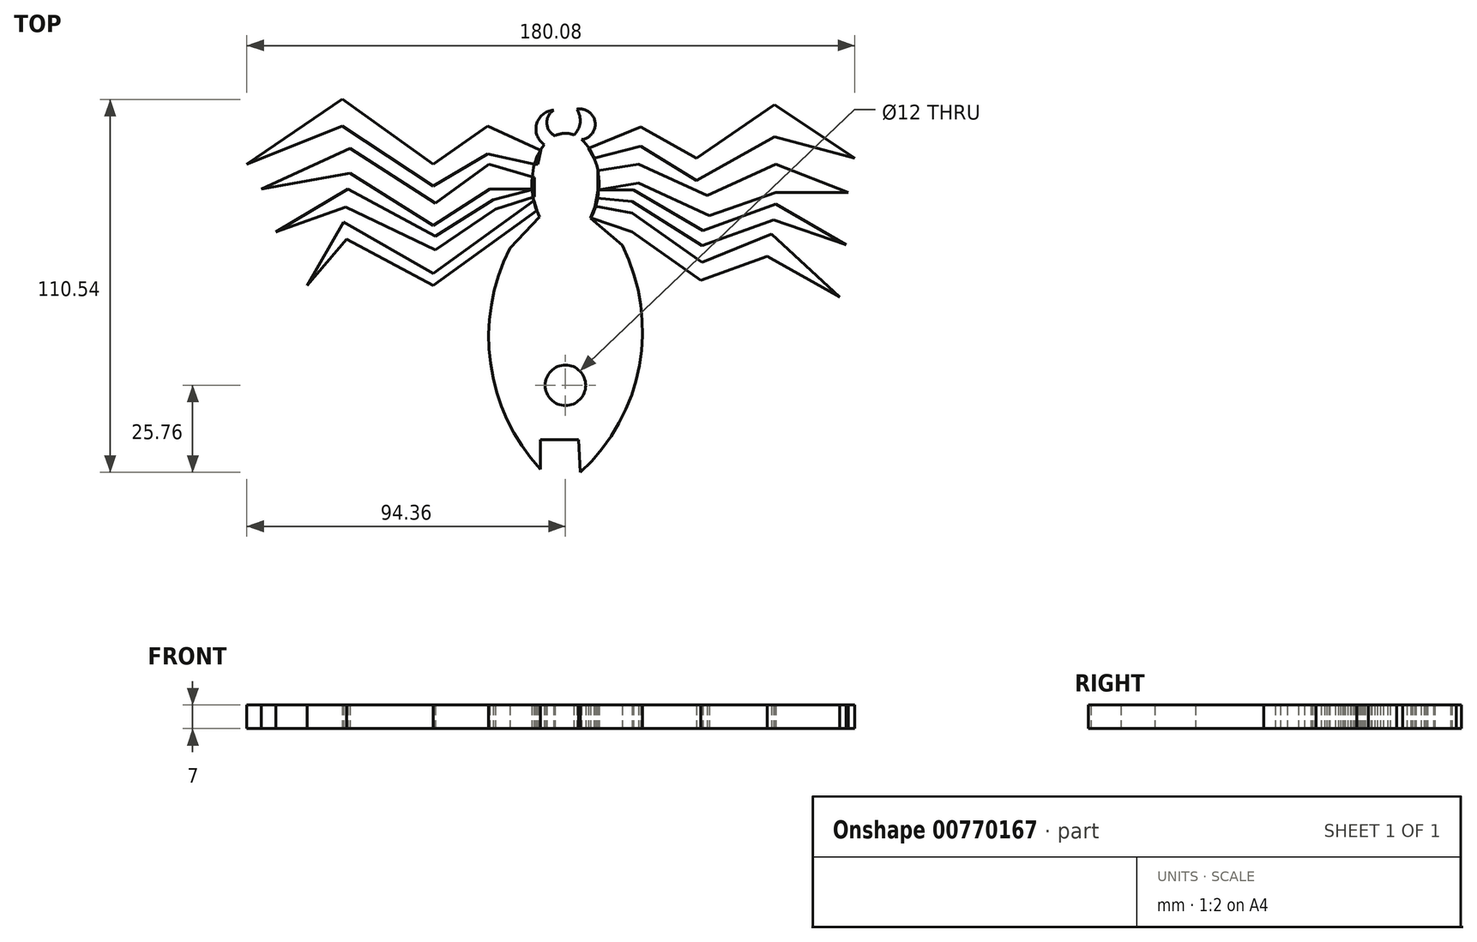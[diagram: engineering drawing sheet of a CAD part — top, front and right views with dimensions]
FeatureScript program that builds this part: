
annotation { "Feature Type Name" : "Feature", "Feature Type Description" : "" }
export const myFeature = defineFeature(function(context is Context, id is Id, definition is map)
    precondition{}
    {
        {
            var Q0;
            Q0=qCreatedBy(makeId("Top.planeOp"),FACE);
            var sketch = newSketch(context, id + "F0", { "sketchPlane" : qUnion([Q0])});
            skEllipse(sketch, "E0", {"center": v(0, 59.61) * mm, "majorRadius": 15.1 * mm, "minorRadius": 9.95 * mm, "majorAxis": v(0, 1)});
            skLineSegment(sketch, "E1", {"start": v(-7.66, 49.96) * mm, "end": v(-16.4, 40.68) * mm});
            skLineSegment(sketch, "E2", {"start": v(7.4, 49.5) * mm, "end": v(16.79, 41.5) * mm});
            skArc(sketch, "E3", {"start": v(-16.4, 40.68) * mm, "mid": v(-22.18, 6.45) * mm, "end": v(-7.36, -24.94) * mm});
            skArc(sketch, "E4", {"start": v(4.44, -25.76) * mm, "mid": v(21.9, 5.8) * mm, "end": v(16.79, 41.5) * mm});
            skLineSegment(sketch, "E5", {"start": v(-7.36, -24.94) * mm, "end": v(-7.36, -16.15) * mm});
            skLineSegment(sketch, "E6", {"start": v(-7.36, -16.15) * mm, "end": v(3.9, -16.15) * mm});
            skLineSegment(sketch, "E7", {"start": v(3.9, -16.15) * mm, "end": v(4.44, -25.76) * mm});
            skArc(sketch, "E8", {"start": v(-3.53, 81.58) * mm, "mid": v(-8.55, 77.44) * mm, "end": v(-6.26, 71.35) * mm});
            skArc(sketch, "E9", {"start": v(4.8, 72.85) * mm, "mid": v(8.77, 78.1) * mm, "end": v(3.34, 81.85) * mm});
            skArc(sketch, "E10", {"start": v(-3.53, 81.58) * mm, "mid": v(-5.49, 77.65) * mm, "end": v(-3.15, 73.93) * mm});
            skArc(sketch, "E11", {"start": v(0, 72.85) * mm, "mid": v(4.01, 76.48) * mm, "end": v(3.34, 81.85) * mm});
            skCircle(sketch, "E12", {"center": v(0, 0) * mm, "radius": 6 * mm});
            skSolve(sketch);
        }
        {
            var Q0;
            Q0=qCreatedBy(makeId("Top.planeOp"),FACE);
            var sketch = newSketch(context, id + "F1", { "sketchPlane" : qUnion([Q0])});
            skLineSegment(sketch, "E13", {"start": v(-7.74, 69.88) * mm, "end": v(-22.97, 76.86) * mm});
            skLineSegment(sketch, "E14", {"start": v(-22.97, 76.86) * mm, "end": v(-39.13, 65.6) * mm});
            skLineSegment(sketch, "E15", {"start": v(-39.13, 65.6) * mm, "end": v(-66.07, 84.78) * mm});
            skLineSegment(sketch, "E16", {"start": v(-66.07, 84.78) * mm, "end": v(-94.36, 65.6) * mm});
            skLineSegment(sketch, "E17", {"start": v(-94.36, 65.6) * mm, "end": v(-66.07, 76.86) * mm});
            skLineSegment(sketch, "E18", {"start": v(-66.07, 76.86) * mm, "end": v(-39.13, 59.12) * mm});
            skLineSegment(sketch, "E19", {"start": v(-39.13, 59.12) * mm, "end": v(-22.97, 68.62) * mm});
            skLineSegment(sketch, "E20", {"start": v(-22.97, 68.62) * mm, "end": v(-9.2, 65.6) * mm});
            skLineSegment(sketch, "E21", {"start": v(6.81, 70.2) * mm, "end": v(22.34, 76.54) * mm});
            skLineSegment(sketch, "E22", {"start": v(22.34, 76.54) * mm, "end": v(38.82, 67.35) * mm});
            skLineSegment(sketch, "E23", {"start": v(38.82, 67.35) * mm, "end": v(61.95, 83.2) * mm});
            skLineSegment(sketch, "E24", {"start": v(61.95, 83.2) * mm, "end": v(85.72, 67.35) * mm});
            skLineSegment(sketch, "E25", {"start": v(85.72, 67.35) * mm, "end": v(61.95, 73.7) * mm});
            skLineSegment(sketch, "E26", {"start": v(61.95, 73.7) * mm, "end": v(38.82, 60.7) * mm});
            skLineSegment(sketch, "E27", {"start": v(38.82, 60.7) * mm, "end": v(22.34, 70.84) * mm});
            skLineSegment(sketch, "E28", {"start": v(22.34, 70.84) * mm, "end": v(8.4, 67.35) * mm});
            skLineSegment(sketch, "E29", {"start": v(-9.2, 61.66) * mm, "end": v(-22.69, 65.6) * mm});
            skLineSegment(sketch, "E30", {"start": v(-22.69, 65.6) * mm, "end": v(-38.5, 54.05) * mm});
            skLineSegment(sketch, "E31", {"start": v(-38.5, 54.05) * mm, "end": v(-63.85, 70.2) * mm});
            skLineSegment(sketch, "E32", {"start": v(-63.85, 70.2) * mm, "end": v(-90.15, 58.17) * mm});
            skLineSegment(sketch, "E33", {"start": v(-90.15, 58.17) * mm, "end": v(-63.85, 62.92) * mm});
            skLineSegment(sketch, "E34", {"start": v(-63.85, 62.92) * mm, "end": v(-39.13, 47.4) * mm});
            skLineSegment(sketch, "E35", {"start": v(-39.13, 47.4) * mm, "end": v(-22.34, 58.17) * mm});
            skLineSegment(sketch, "E36", {"start": v(-22.34, 58.17) * mm, "end": v(-9.2, 58.17) * mm});
            skLineSegment(sketch, "E37", {"start": v(9.66, 63.6) * mm, "end": v(21.7, 65.6) * mm});
            skLineSegment(sketch, "E38", {"start": v(21.7, 65.6) * mm, "end": v(42, 56.3) * mm});
            skLineSegment(sketch, "E39", {"start": v(42, 56.3) * mm, "end": v(62.27, 65.6) * mm});
            skLineSegment(sketch, "E40", {"start": v(62.27, 65.6) * mm, "end": v(83.82, 57.21) * mm});
            skLineSegment(sketch, "E41", {"start": v(83.82, 57.21) * mm, "end": v(62.27, 57.21) * mm});
            skLineSegment(sketch, "E42", {"start": v(62.27, 57.21) * mm, "end": v(42.69, 50.3) * mm});
            skLineSegment(sketch, "E43", {"start": v(42.69, 50.3) * mm, "end": v(21.7, 59.9) * mm});
            skLineSegment(sketch, "E44", {"start": v(21.7, 59.9) * mm, "end": v(9.61, 57.9) * mm});
            skLineSegment(sketch, "E45", {"start": v(-9.2, 58.17) * mm, "end": v(-21.39, 55) * mm});
            skLineSegment(sketch, "E46", {"start": v(-21.39, 55) * mm, "end": v(-38.5, 44.22) * mm});
            skLineSegment(sketch, "E47", {"start": v(-38.5, 44.22) * mm, "end": v(-64.49, 58.17) * mm});
            skLineSegment(sketch, "E48", {"start": v(-64.49, 58.17) * mm, "end": v(-85.72, 45.5) * mm});
            skLineSegment(sketch, "E49", {"start": v(-85.72, 45.5) * mm, "end": v(-65.12, 52.78) * mm});
            skLineSegment(sketch, "E50", {"start": v(-65.12, 52.78) * mm, "end": v(-38.5, 40.1) * mm});
            skLineSegment(sketch, "E51", {"start": v(-38.5, 40.1) * mm, "end": v(-20.76, 52.14) * mm});
            skLineSegment(sketch, "E52", {"start": v(9.61, 57.9) * mm, "end": v(20.2, 57.9) * mm});
            skLineSegment(sketch, "E53", {"start": v(20.2, 57.9) * mm, "end": v(40.72, 45.8) * mm});
            skLineSegment(sketch, "E54", {"start": v(40.72, 45.8) * mm, "end": v(62.27, 53.73) * mm});
            skLineSegment(sketch, "E55", {"start": v(62.27, 53.73) * mm, "end": v(83.18, 41.69) * mm});
            skLineSegment(sketch, "E56", {"start": v(83.18, 41.69) * mm, "end": v(61.63, 48.98) * mm});
            skLineSegment(sketch, "E57", {"start": v(61.63, 48.98) * mm, "end": v(40.4, 41.37) * mm});
            skLineSegment(sketch, "E58", {"start": v(40.4, 41.37) * mm, "end": v(19.8, 54.55) * mm});
            skLineSegment(sketch, "E59", {"start": v(-9.35, 54.69) * mm, "end": v(-39.13, 33.13) * mm});
            skLineSegment(sketch, "E60", {"start": v(-39.13, 33.13) * mm, "end": v(-65.75, 48.34) * mm});
            skLineSegment(sketch, "E61", {"start": v(-65.75, 48.34) * mm, "end": v(-76.44, 29.64) * mm});
            skLineSegment(sketch, "E62", {"start": v(-76.44, 29.64) * mm, "end": v(-64.8, 43.27) * mm});
            skLineSegment(sketch, "E63", {"start": v(-64.8, 43.27) * mm, "end": v(-39.13, 29.64) * mm});
            skLineSegment(sketch, "E64", {"start": v(-39.13, 29.64) * mm, "end": v(-8.47, 51.83) * mm});
            skLineSegment(sketch, "E65", {"start": v(19.8, 51.12) * mm, "end": v(40.4, 36.45) * mm});
            skLineSegment(sketch, "E66", {"start": v(40.4, 36.45) * mm, "end": v(61, 44.86) * mm});
            skLineSegment(sketch, "E67", {"start": v(61, 44.86) * mm, "end": v(81.28, 26.16) * mm});
            skLineSegment(sketch, "E68", {"start": v(81.28, 26.16) * mm, "end": v(59.73, 38.2) * mm});
            skLineSegment(sketch, "E69", {"start": v(59.73, 38.2) * mm, "end": v(40.06, 31.1) * mm});
            skLineSegment(sketch, "E70", {"start": v(40.06, 31.1) * mm, "end": v(19.8, 45.53) * mm});
            skLineSegment(sketch, "E71", {"start": v(19.8, 45.53) * mm, "end": v(8.07, 49.4) * mm});
            skLineSegment(sketch, "E72", {"start": v(19.8, 51.12) * mm, "end": v(8.83, 53.1) * mm});
            skLineSegment(sketch, "E73", {"start": v(8.83, 53.1) * mm, "end": v(9.61, 57.9) * mm});
            skLineSegment(sketch, "E74", {"start": v(6.81, 70.2) * mm, "end": v(8.4, 67.35) * mm});
            skLineSegment(sketch, "E75", {"start": v(8.4, 67.35) * mm, "end": v(9.66, 63.6) * mm});
            skLineSegment(sketch, "E76", {"start": v(9.66, 63.6) * mm, "end": v(9.61, 57.9) * mm});
            skLineSegment(sketch, "E77", {"start": v(8.07, 49.4) * mm, "end": v(8.83, 53.1) * mm});
            skLineSegment(sketch, "E78", {"start": v(-9.35, 54.69) * mm, "end": v(-8.47, 51.83) * mm});
            skLineSegment(sketch, "E79", {"start": v(-9.2, 61.66) * mm, "end": v(-9.2, 58.17) * mm});
            skLineSegment(sketch, "E80", {"start": v(-7.74, 69.88) * mm, "end": v(-9.2, 65.6) * mm});
            skLineSegment(sketch, "E81", {"start": v(-7.6, 69.88) * mm, "end": v(-7.74, 69.88) * mm});
            skLineSegment(sketch, "E82", {"start": v(-7.74, 69.88) * mm, "end": v(-8.69, 65.6) * mm});
            skLineSegment(sketch, "E83", {"start": v(-8.69, 65.6) * mm, "end": v(-9.2, 65.6) * mm});
            skLineSegment(sketch, "E84", {"start": v(19.8, 54.55) * mm, "end": v(9.22, 55.5) * mm});
            skLineSegment(sketch, "E85", {"start": v(9.22, 55.5) * mm, "end": v(8.07, 49.4) * mm});
            skLineSegment(sketch, "E86", {"start": v(8.07, 49.4) * mm, "end": v(7.4, 49.61) * mm});
            skLineSegment(sketch, "E87", {"start": v(7.4, 49.61) * mm, "end": v(8.83, 53.1) * mm});
            skLineSegment(sketch, "E88", {"start": v(-20.76, 52.14) * mm, "end": v(-9.2, 55.89) * mm});
            skLineSegment(sketch, "E89", {"start": v(-9.2, 55.89) * mm, "end": v(-9.2, 58.17) * mm});
            skLineSegment(sketch, "E90", {"start": v(-7.74, 69.88) * mm, "end": v(-7.26, 69.78) * mm});
            skLineSegment(sketch, "E91", {"start": v(-7.26, 69.78) * mm, "end": v(-8.17, 65.6) * mm});
            skLineSegment(sketch, "E92", {"start": v(-8.17, 65.6) * mm, "end": v(-8.69, 65.6) * mm});
            skSolve(sketch);
        }
        {
            var Q0;
            Q0 = qSketchRegion(id + "F1", true);
            var Q1;
            Q1 = qSketchRegion(id + "F0", true);
            extrude(context, id + "F2", {"entities" : qUnion([Q0, Q1]), "depth" : 7 * mm, "offsetDistance" : 25 * mm});
        }
    });
